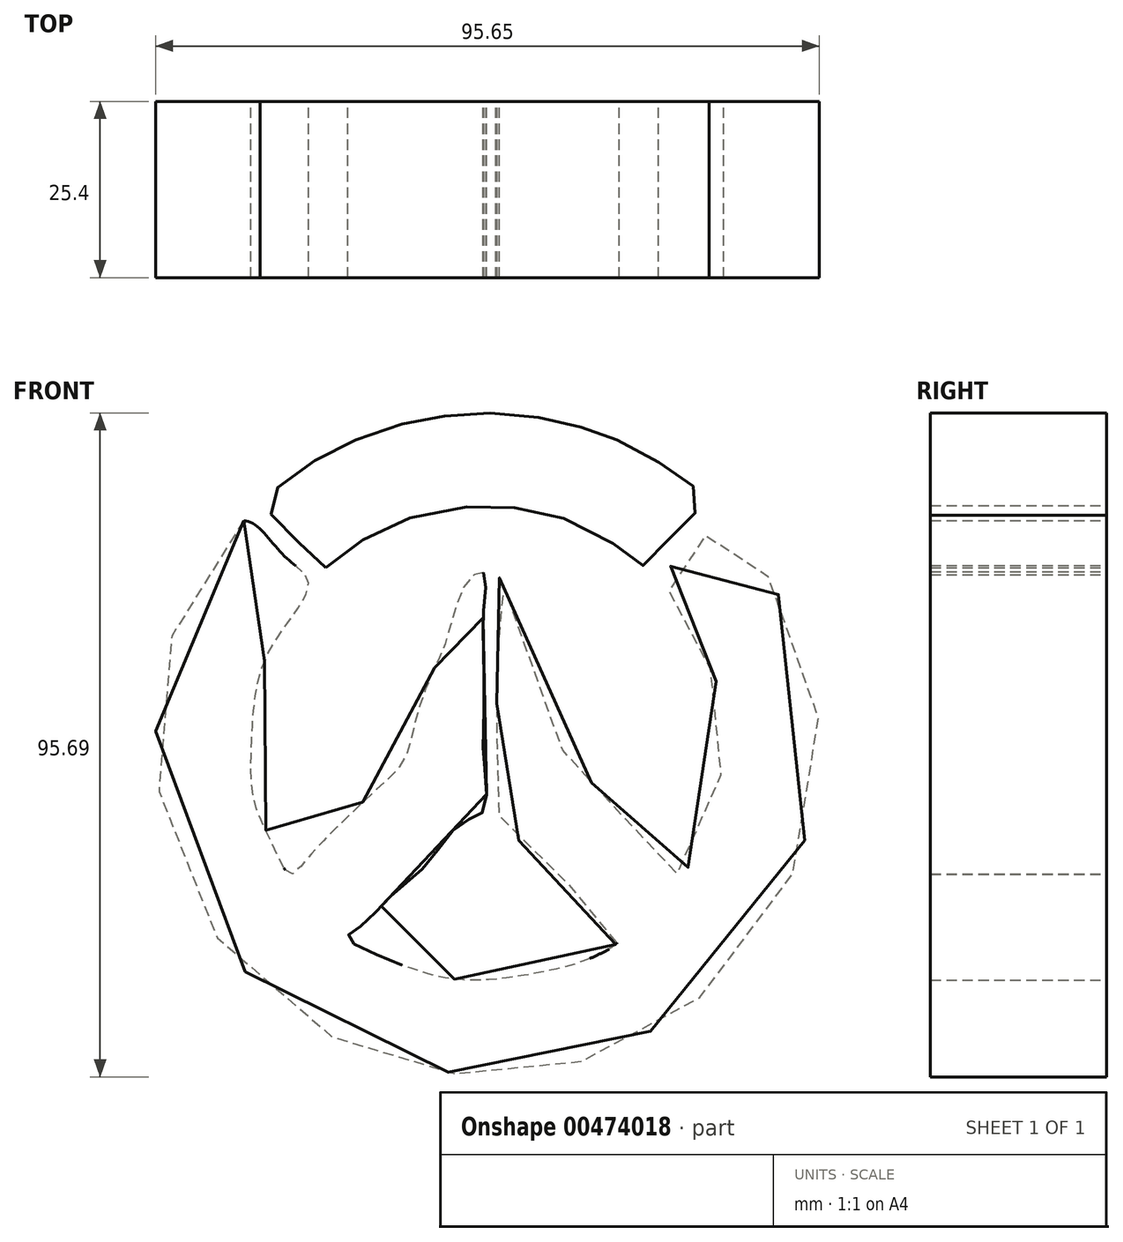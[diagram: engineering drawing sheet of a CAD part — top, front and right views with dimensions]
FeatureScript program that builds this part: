
annotation { "Feature Type Name" : "Feature", "Feature Type Description" : "" }
export const myFeature = defineFeature(function(context is Context, id is Id, definition is map)
    precondition{}
    {
        {
            var Q0;
            Q0=qCreatedBy(makeId("Front.planeOp"),FACE);
            var sketch = newSketch(context, id + "F0", { "sketchPlane" : qUnion([Q0])});
            skFitSpline(sketch, "E0", {"points": [v(-34.58, 25.87) * mm, v(-41.81, 16.48) * mm, v(-46.37, 3.89) * mm, v(-46.64, -14.07) * mm, v(-41.01, -30.15) * mm, v(-31.1, -42.22) * mm, v(-17.96, -50.26) * mm, v(-6.97, -53.2) * mm, v(0, -54.28) * mm, v(12.87, -52.4) * mm, v(23.32, -48.11) * mm, v(34.58, -39.8) * mm, v(43.96, -26.4) * mm, v(48.25, -9.78) * mm, v(46.64, 6.03) * mm, v(39.94, 19.7) * mm, v(34.58, 26.67) * mm, v(32.16, 23.99) * mm, v(28.41, 20.24) * mm, v(25.2, 17.56) * mm, v(27.6, 14.88) * mm, v(29.75, 10.59) * mm, v(32.16, 5.5) * mm, v(34.3, 0) * mm, v(34.3, -9.25) * mm, v(32.7, -17.82) * mm, v(28.14, -25.06) * mm, v(26.54, -22.92) * mm, v(24.66, -21.04) * mm, v(20.1, -16.75) * mm, v(15.28, -11.66) * mm, v(12.33, -8.98) * mm, v(9.11, 0) * mm, v(1.88, 18.1) * mm, v(2.14, 13.54) * mm, v(2.14, 8.71) * mm, v(1.88, 2.28) * mm, v(1.88, 0) * mm, v(1.88, -6.03) * mm, v(1.88, -13) * mm, v(1.88, -15.68) * mm, v(4.02, -19.16) * mm, v(8.85, -23.45) * mm, v(14.74, -29.35) * mm, v(17.7, -33.1) * mm, v(19.57, -34.44) * mm, v(15.55, -37.12) * mm, v(10.45, -38.73) * mm, v(2.95, -40.07) * mm, v(-5.1, -40.07) * mm, v(-13.67, -37.4) * mm, v(-19.57, -34.18) * mm, v(-17.7, -32.57) * mm, v(-13.13, -28.01) * mm, v(-8.3, -23.72) * mm, v(-2.95, -17.56) * mm, v(0, -15.95) * mm, v(0, -8.44) * mm, v(0, -3.62) * mm, v(0, 7.1) * mm, v(0, 13) * mm, v(0, 18.36) * mm, v(-2.41, 17.02) * mm, v(-5.36, 8.71) * mm, v(-7.77, 3.08) * mm, v(-9.92, -3.35) * mm, v(-11.53, -8.71) * mm, v(-15.28, -12.73) * mm, v(-20.64, -17.82) * mm, v(-25.73, -23.19) * mm, v(-27.88, -25.06) * mm, v(-30.29, -21.04) * mm, v(-32.97, -14.88) * mm, v(-33.5, -8.44) * mm, v(-32.97, 0) * mm, v(-30.29, 8.18) * mm, v(-25.2, 16.75) * mm, v(-28.68, 20.77) * mm, v(-34.58, 25.87) * mm]});
            skFitSpline(sketch, "E1", {"points": [v(-51.46, 29.89) * mm, v(-48.25, 30.42) * mm], "startDerivative": vector(3.22, 0.54) * mm, "endDerivative": vector(3.22, 0.54) * mm});
            skFitSpline(sketch, "E2", {"points": [v(-22.77, 19.07) * mm, v(-20.89, 20.64) * mm, v(-17.54, 23.05) * mm, v(-14.03, 24.94) * mm, v(-9.63, 26.56) * mm, v(-4.4, 27.6) * mm, v(0, 28.02) * mm, v(3.3, 27.87) * mm, v(7.17, 27.3) * mm, v(10.94, 26.4) * mm, v(15.07, 24.67) * mm, v(19.1, 22.32) * mm, v(21.2, 21) * mm, v(22.92, 19.44) * mm, v(22.95, 19.41) * mm, v(24.25, 20.68) * mm, v(26, 22.47) * mm, v(27.22, 23.65) * mm, v(28.18, 24.59) * mm, v(29.49, 25.99) * mm, v(32.46, 28.85) * mm, v(32.46, 28.92) * mm, v(31.03, 30.17) * mm, v(28.52, 32.1) * mm, v(26.52, 33.5) * mm, v(23.94, 35.1) * mm, v(20.83, 36.79) * mm, v(17.8, 38.11) * mm, v(16.4, 38.58) * mm, v(13.9, 39.42) * mm, v(11.5, 39.97) * mm, v(8.23, 40.72) * mm, v(4.95, 41.22) * mm, v(0.9, 41.4) * mm, v(-2, 41.31) * mm, v(-5.64, 40.95) * mm, v(-8.48, 40.64) * mm, v(-11.28, 39.92) * mm, v(-15.11, 38.92) * mm, v(-18.31, 37.57) * mm, v(-21.38, 36.26) * mm, v(-24.18, 34.64) * mm, v(-26.57, 33.06) * mm, v(-29.23, 31.03) * mm, v(-32.16, 28.55) * mm, v(-32.16, 28.42) * mm, v(-30.71, 26.89) * mm, v(-29.27, 25.3) * mm, v(-27.38, 23.46) * mm, v(-25.62, 21.8) * mm, v(-23.77, 19.99) * mm, v(-22.77, 19.07) * mm]});
            skSolve(sketch);
        }
        {
            var Q0;
            Q0=makeQuery(id+"F0.imprint","IMPRINT",FACE,{"disambiguationData":[TD([[makeQuery(id+"F0.imprint","IMPRINT",EDGE,{"derivedFrom":sQuery(id+"F0.wireOp",EDGE,"E0")}),1.0]])]});
            extrude(context, id + "F1", {"entities" : qUnion([Q0]), "depth" : 25.4 * mm});
        }
        {
            var Q0;
            Q0 = qSketchRegion(id + "F0", true);
            extrude(context, id + "F2", {"entities" : qUnion([Q0]), "operationType" : NewBodyOperationType.ADD, "depth" : 25.4 * mm});
        }
    });
